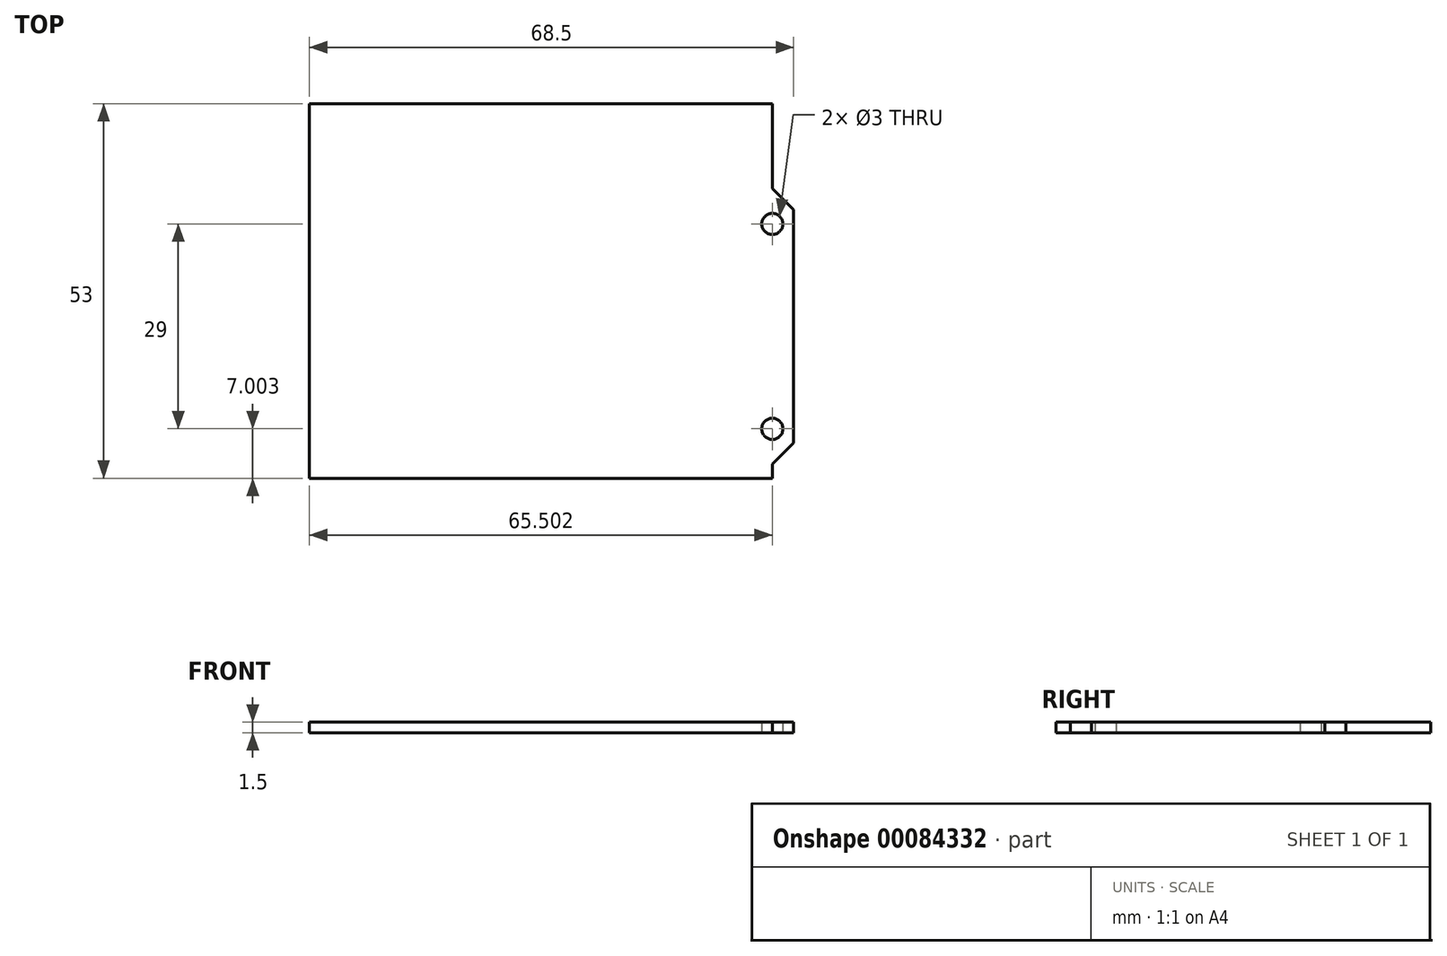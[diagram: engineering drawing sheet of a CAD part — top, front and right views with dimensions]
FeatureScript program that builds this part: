
annotation { "Feature Type Name" : "Feature", "Feature Type Description" : "" }
export const myFeature = defineFeature(function(context is Context, id is Id, definition is map)
    precondition{}
    {
        {
            var Q0;
            Q0=qCreatedBy(makeId("Top.planeOp"),FACE);
            var sketch = newSketch(context, id + "F0", { "sketchPlane" : qUnion([Q0])});
            skLineSegment(sketch, "E0.bottom", {"start": v(-37.06, 68.97) * mm, "end": v(28.44, 68.97) * mm});
            skLineSegment(sketch, "E0.top", {"start": v(-37.06, 15.97) * mm, "end": v(28.44, 15.97) * mm});
            skLineSegment(sketch, "E0.left", {"start": v(-37.06, 68.97) * mm, "end": v(-37.06, 15.97) * mm});
            skLineSegment(sketch, "E0.right", {"start": v(28.44, 68.97) * mm, "end": v(28.44, 56.97) * mm});
            skLineSegment(sketch, "E1", {"start": v(28.44, 17.97) * mm, "end": v(31.44, 20.97) * mm});
            skLineSegment(sketch, "E2", {"start": v(31.44, 20.97) * mm, "end": v(31.44, 53.97) * mm});
            skLineSegment(sketch, "E3", {"start": v(31.44, 53.97) * mm, "end": v(28.44, 56.97) * mm});
            skPoint(sketch, "E4", {"position": v(28.44, 22.97) * mm});
            skCircle(sketch, "E5", {"center": v(28.44, 22.97) * mm, "radius": 1.5 * mm});
            skPoint(sketch, "E6", {"position": v(28.44, 51.97) * mm});
            skCircle(sketch, "E7", {"center": v(28.44, 51.97) * mm, "radius": 1.5 * mm});
            skLineSegment(sketch, "E8.trimOffspring", {"start": v(28.44, 17.97) * mm, "end": v(28.44, 15.97) * mm});
            skSolve(sketch);
        }
        {
            var Q0;
            Q0=makeQuery(id+"F0.imprint","IMPRINT",FACE,{"disambiguationData":[TD([[makeQuery(id+"F0.imprint","IMPRINT",EDGE,{"derivedFrom":sQuery(id+"F0.wireOp",EDGE,"E0.bottom")}),-1.0]])]});
            extrude(context, id + "F1", {"entities" : qUnion([Q0]), "depth" : 1.5 * mm});
        }
    });
